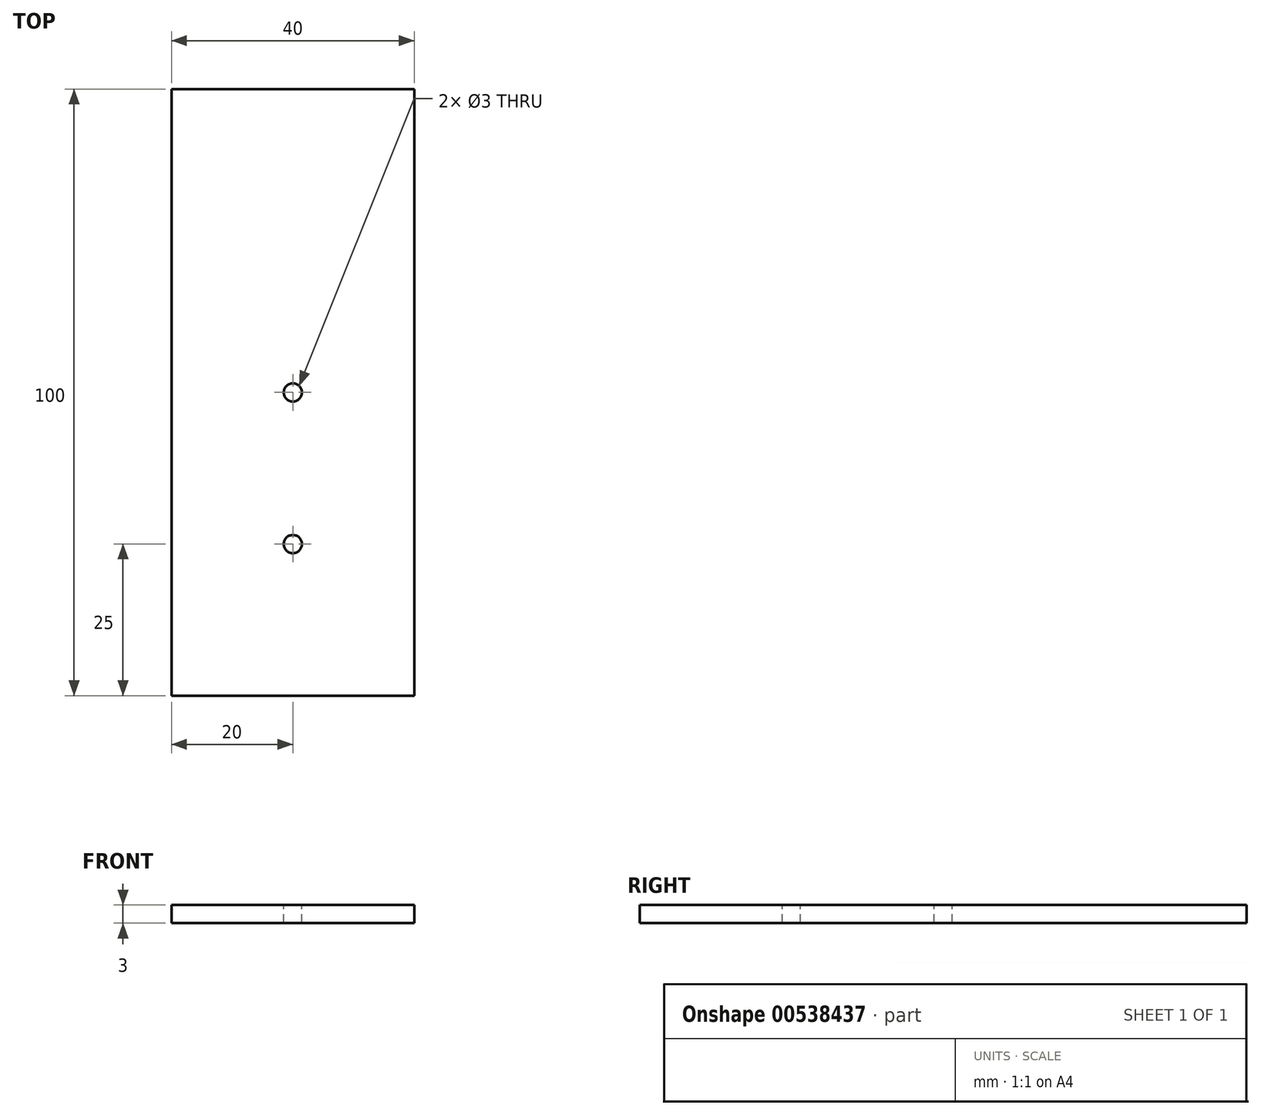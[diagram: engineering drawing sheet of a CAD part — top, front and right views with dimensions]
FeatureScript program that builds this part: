
annotation { "Feature Type Name" : "Feature", "Feature Type Description" : "" }
export const myFeature = defineFeature(function(context is Context, id is Id, definition is map)
    precondition{}
    {
        {
            var Q0;
            Q0=qCreatedBy(makeId("Top.planeOp"),FACE);
            var sketch = newSketch(context, id + "F0", { "sketchPlane" : qUnion([Q0])});
            skLineSegment(sketch, "E0.bottom", {"start": v(0, 0) * mm, "end": v(40, 0) * mm});
            skLineSegment(sketch, "E0.top", {"start": v(0, 100) * mm, "end": v(40, 100) * mm});
            skLineSegment(sketch, "E0.left", {"start": v(0, 0) * mm, "end": v(0, 100) * mm});
            skLineSegment(sketch, "E0.right", {"start": v(40, 0) * mm, "end": v(40, 100) * mm});
            skSolve(sketch);
        }
        {
            var Q0;
            Q0=makeQuery(id+"F0.imprint","IMPRINT",FACE,{"disambiguationData":[TD([[makeQuery(id+"F0.imprint","IMPRINT",EDGE,{"derivedFrom":sQuery(id+"F0.wireOp",EDGE,"E0.bottom")}),1.0]])]});
            extrude(context, id + "F1", {"entities" : qUnion([Q0]), "depth" : 3 * mm, "offsetDistance" : 25 * mm});
        }
        {
            var Q0;
            Q0=makeQuery(id+"F1.opExtrude","CAP_FACE",FACE,{"disambiguationData":[OSD([sQuery(id+"F0.wireOp",EDGE,"E0.bottom"),sQuery(id+"F0.wireOp",EDGE,"E0.top"),sQuery(id+"F0.wireOp",EDGE,"E0.left"),sQuery(id+"F0.wireOp",EDGE,"E0.right")])],"isStart":false});
            var sketch = newSketch(context, id + "F2", { "sketchPlane" : qUnion([Q0])});
            skLineSegment(sketch, "E1", {"start": v(20, 50) * mm, "end": v(20, 25) * mm});
            skSolve(sketch);
        }
        {
            var Q0;
            Q0=sQuery(id+"F2.wireOp",VERTEX,"E1.start");
            var Q1;
            Q1=sQuery(id+"F2.wireOp",VERTEX,"E1.end");
            var Q2;
            Q2=makeQuery(id+"F1.opExtrude","SWEPT_BODY",BODY,{"disambiguationData":[OSD([sQuery(id+"F0.wireOp",EDGE,"E0.bottom"),sQuery(id+"F0.wireOp",EDGE,"E0.top"),sQuery(id+"F0.wireOp",EDGE,"E0.left"),sQuery(id+"F0.wireOp",EDGE,"E0.right")])]});
            hole(context, id + "F3", {"style" : HoleStyle.SIMPLE, "endStyle" : HoleEndStyle.THROUGH, "holeDiameter" : 3 * mm, "isTappedThrough" : true, "tappedDepth" : 12 * mm, "tapClearance" : 3, "locations" : qUnion([Q0, Q1]), "scope" : qUnion([Q2])});
        }
    });
